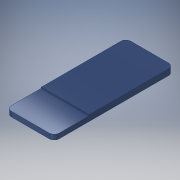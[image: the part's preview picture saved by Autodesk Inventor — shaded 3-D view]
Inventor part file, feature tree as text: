
AUTODESK INVENTOR PART (.ipt)
format: ipt  version: 2019 (Build 230136000, 136)  size: 117,248 bytes
history: native  units: in
note: dims shown in document units (in); Inventor stores cm internally (conversion verified against a paired STEP export)
features: extrude x2, sketch x2
ambient origin geometry x8: Origin, YZ Plane, XZ Plane, XY Plane, X Axis, Y Axis, Z Axis, Center Point
bodies: Solid1 (feature_tree)
feature tree (4):
  extrude  "Extrusion1"  Depth=1.2in
  extrude  "Extrusion2"  Depth=0.06in TaperAngle=0.0deg
  sketch  "Sketch1"  dims[d0=0.48in d1=1.2in]
  sketch  "Sketch2"  dims[d2=0.05in d3=0.06in d4=0.0in d5=0.35in d6=0.48in d7=0.38in d8=0.01in d9=0.0in]
